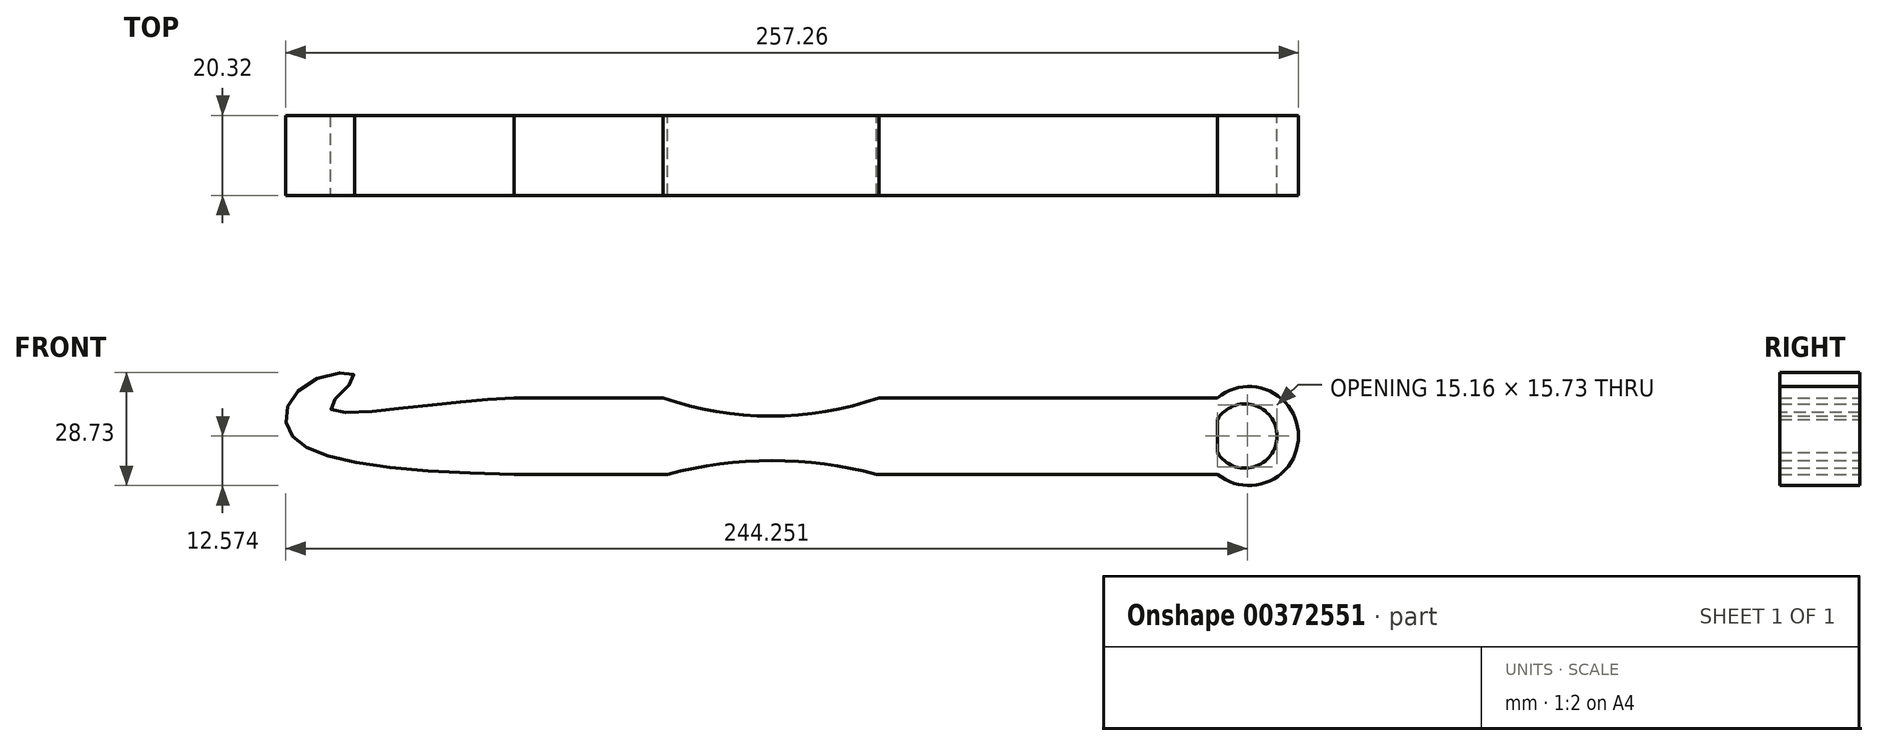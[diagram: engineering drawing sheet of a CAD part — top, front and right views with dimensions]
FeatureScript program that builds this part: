
annotation { "Feature Type Name" : "Feature", "Feature Type Description" : "" }
export const myFeature = defineFeature(function(context is Context, id is Id, definition is map)
    precondition{}
    {
        {
            var Q0;
            Q0=qCreatedBy(makeId("Front.planeOp"),FACE);
            var sketch = newSketch(context, id + "F0", { "sketchPlane" : qUnion([Q0])});
            skLineSegment(sketch, "E0.bottom", {"start": v(-64.5, -19.4) * mm, "end": v(114.24, -19.4) * mm});
            skLineSegment(sketch, "E0.top", {"start": v(-64.5, 0) * mm, "end": v(114.24, 0) * mm});
            skLineSegment(sketch, "E0.left", {"start": v(-64.5, -19.4) * mm, "end": v(-64.5, 0) * mm});
            skLineSegment(sketch, "E0.right", {"start": v(114.24, -19.4) * mm, "end": v(114.24, 0) * mm});
            skArc(sketch, "E1", {"start": v(114.24, -19.4) * mm, "mid": v(134.83, -9.7) * mm, "end": v(114.24, 0) * mm});
            skArc(sketch, "E2", {"start": v(114.24, -13.91) * mm, "mid": v(129.4, -9.7) * mm, "end": v(114.24, -5.48) * mm});
            skFitSpline(sketch, "E3", {"points": [v(-64.5, -19.4) * mm, v(-114.24, -13.91) * mm, v(-122.32, -6.33) * mm, v(-116.77, 3.8) * mm, v(-104.97, 5.48) * mm, v(-111.14, -2.15) * mm, v(-94.15, -2.75) * mm, v(-64.5, 0) * mm], "startDerivative": vector(-261.84, 5.67) * mm, "endDerivative": vector(154.16, 7.14) * mm});
            skArc(sketch, "E4", {"start": v(-26.64, 0) * mm, "mid": v(0.79, -4.65) * mm, "end": v(28.2, 0) * mm});
            skArc(sketch, "E5", {"start": v(27.61, -19.4) * mm, "mid": v(1.08, -15.95) * mm, "end": v(-25.45, -19.4) * mm});
            skSolve(sketch);
        }
        {
            var Q0;
            Q0=makeQuery(id+"F0.imprint","IMPRINT",FACE,{"disambiguationData":[TD([[makeQuery(id+"F0.imprint","IMPRINT",EDGE,{"derivedFrom":sQuery(id+"F0.wireOp",EDGE,"E0.left")}),1.0]])]});
            var Q1;
            {var subQ1=sQuery(id+"F0.wireOp",EDGE,"E0.left");Q1=makeQuery(id+"F0.imprint","IMPRINT",FACE,{"disambiguationData":[TD([[makeQuery(id+"F0.imprint","IMPRINT",EDGE,{"derivedFrom":subQ1}),-1.0]])]});}
            var Q2;
            {var subQ0=sQuery(id+"F0.wireOp",EDGE,"E1");Q2=makeQuery(id+"F0.imprint","IMPRINT",FACE,{"disambiguationData":[TD([[makeQuery(id+"F0.imprint","IMPRINT",EDGE,{"derivedFrom":subQ0}),1.0]])]});}
            extrude(context, id + "F1", {"entities" : qUnion([Q0, Q1, Q2]), "endBound" : BoundingType.SYMMETRIC, "depth" : 20.32 * mm});
        }
    });
